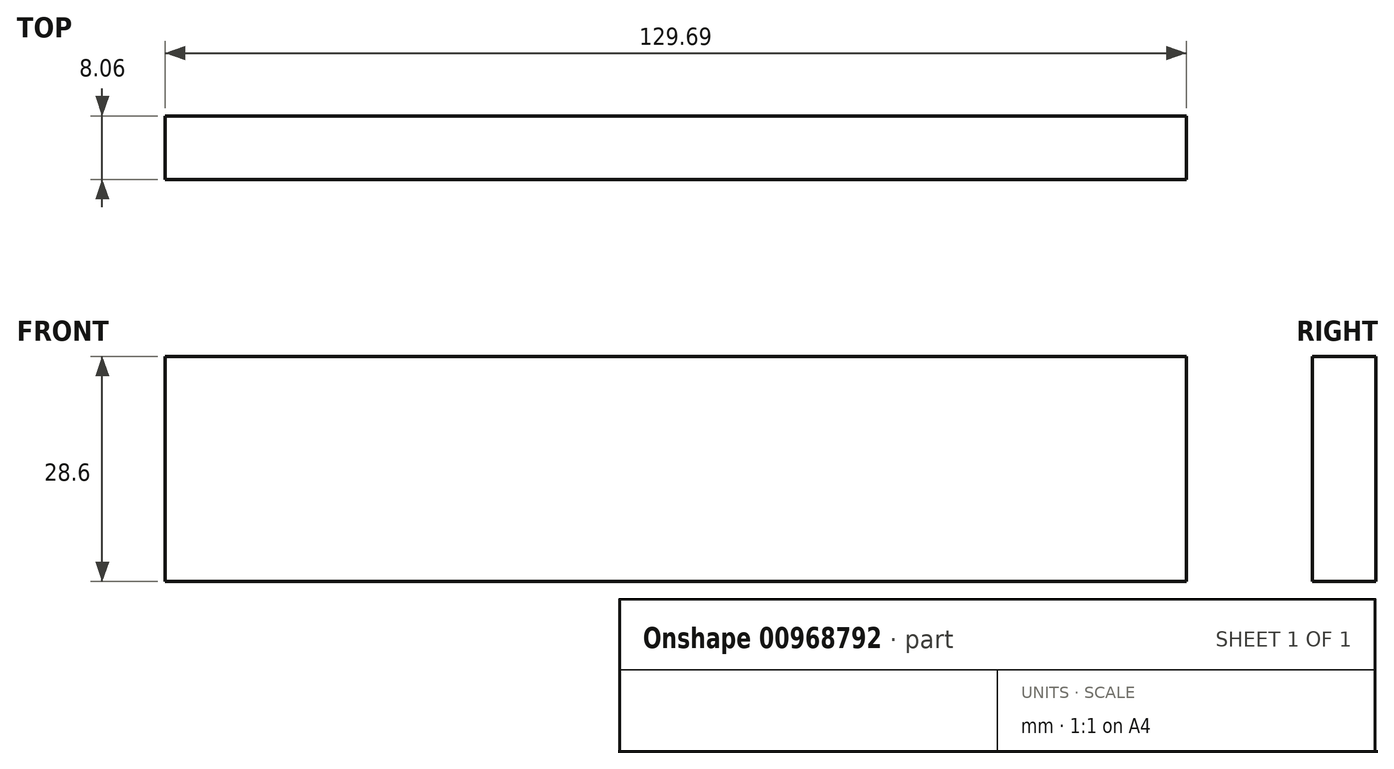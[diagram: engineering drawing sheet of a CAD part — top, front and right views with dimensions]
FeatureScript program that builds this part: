
annotation { "Feature Type Name" : "Feature", "Feature Type Description" : "" }
export const myFeature = defineFeature(function(context is Context, id is Id, definition is map)
    precondition{}
    {
        {
            var Q0;
            Q0=qCreatedBy(makeId("Front.planeOp"),FACE);
            var sketch = newSketch(context, id + "F0", { "sketchPlane" : qUnion([Q0])});
            skLineSegment(sketch, "E0.bottom", {"start": v(62.88, 0) * mm, "end": v(-66.81, 0) * mm});
            skLineSegment(sketch, "E0.top", {"start": v(62.88, -28.6) * mm, "end": v(-66.81, -28.6) * mm});
            skLineSegment(sketch, "E0.left", {"start": v(62.88, 0) * mm, "end": v(62.88, -28.6) * mm});
            skLineSegment(sketch, "E0.right", {"start": v(-66.81, 0) * mm, "end": v(-66.81, -28.6) * mm});
            skSolve(sketch);
        }
        {
            var Q0;
            Q0=makeQuery(id+"F0.imprint","IMPRINT",FACE,{"disambiguationData":[TD([[makeQuery(id+"F0.imprint","IMPRINT",EDGE,{"derivedFrom":sQuery(id+"F0.wireOp",EDGE,"E0.bottom")}),1.0]])]});
            extrude(context, id + "F1", {"entities" : qUnion([Q0]), "depth" : 8.06 * mm, "offsetDistance" : 25.4 * mm});
        }
    });
